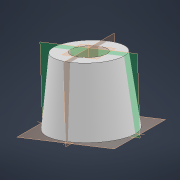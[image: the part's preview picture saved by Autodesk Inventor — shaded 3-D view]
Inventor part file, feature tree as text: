
AUTODESK INVENTOR PART (.ipt)
format: ipt  version: 2021 (Build 250183000, 183)  size: 239,104 bytes
history: native  units: mm
features: sketch x3, plane x1, loft x1, revolve x1
ambient origin geometry x8: Origin, YZ Plane, XZ Plane, XY Plane, X Axis, Y Axis, Z Axis, Center Point
bodies: Solid2 (feature_tree)
feature tree (6):
  sketch  "Sketch1"  dims[d0=50.0mm d14=90.0deg]
  plane  "Work Plane2"
  loft  "Loft2"
  revolve  "Revolution1"  [1 undecoded]
  sketch  "Sketch4"  dims[d15=40.0mm d16=40.0mm]
  sketch  "Sketch5"  dims[d17=0.0mm d18=90.0deg d19=0.0mm d20=90.0deg d22=10.25mm d23=28.0mm d24=6.0mm d26=8.5mm d27=4.75mm]
note: 1 required parameter value undecoded (feature->parameter linkage not recoverable at this tier; creation-order binding heuristic only, values carry confidence <= 0.55)
